# Revit family: BIM Motala Hissar
name_source: partatom
category: Generic Models
units: mm (PartAtom-declared; Revit-internal decimal feet)

## family parameters
Always vertical = Yes
Can host rebar = No
Cut with Voids When Loaded = No
Maintain Annotation Orientation = No
Part Type = Normal
Room Calculation Point = No
Round Connector Dimension = Use Diameter
Shared = No
Work Plane-Based = No

## types (1)
- MasterType
    Default Elevation = 0 mm  [stored 0 ft]
    DoorAutoTypes = 0&34603&34603&0&0&0&0&0&0&0&0&0&0&¤34603&0&0&0&0&0&0&0&0&0&0&0&0&¤0&0&0&0&0&0&0&0&0&0&0&0&0&¤0&0&0&0&0&0&0&0&0&0&0&0&0&¤
    Justerings = 0&0&0&0&0&0&0&0&0&0&0&0&0&¤34401&0&0&0&0&0&0&0&0&0&0&0&0&¤0&0&0&0&0&0&0&0&0&0&0&0&0&¤0&0&0&0&0&0&0&0&0&0&0&0&0&¤
    LeftHangTypes = 0&34101&34101&0&0&0&0&0&0&0&0&0&0&¤34101&0&0&0&0&0&0&0&0&0&0&0&0&¤0&0&0&0&0&0&0&0&0&0&0&0&0&¤0&0&0&0&0&0&0&0&0&0&0&0&0&¤
    doorHeights = 0&2260&2160&0&0&0&0&0&0&0&0&0&0&¤2260&0&2160&0&0&0&0&0&0&0&0&0&0&¤0&0&2160&0&0&0&0&0&0&0&0&0&0&¤0&0&2160&0&0&0&0&0&0&0&0&0&0&¤
    doorWidths = 900&900&900&0&0&0&0&0&0&0&0&0&0&¤1000&900&1000&0&0&0&0&0&0&0&0&0&0&¤900&900&900&0&0&0&0&0&0&0&0&0&0&¤900&900&1000&0&0&0&0&0&0&0&0&0&0&¤
    driveSide = D
    glassLists = <blob elided: 1217 chars, md5=ff18d122>
    glazingOffsets = 0&0&0&0&0&0&0&0&0&0&0&0&0&0&0&0&0&0&0&0&0&0&0&0&0&0&0&0&0&0&0&0&0&0&0&0&0&0&0&0&0&0&0&0&0&0&0&0&0&0&
    intHeights = 2000&2000&2000&0&0&0&0&0&0&0&0&0&0&¤2000&2000&2000&0&0&0&0&0&0&0&0&0&0&¤2000&2000&2000&0&0&0&0&0&0&0&0&0&0&¤2000&2000&2000&0&0&0&0&0&0&0&0&0&0&¤
    noOfStops = 3
    pitDepth = 60 mm  [stored 0.19685 ft]
    shaftDepth = 1560 mm  [stored 5.11811 ft]
    shaftHeight = 8853 mm  [stored 29.0453 ft]
    shaftWidth = 1250 mm  [stored 4.10105 ft]
    types = 0&34004&34006&0&0&0&0&0&0&0&0&0&0&¤34006&0&0&0&0&0&0&0&0&0&0&0&0&¤0&0&0&0&0&0&0&0&0&0&0&0&0&¤0&0&0&0&0&0&0&0&0&0&0&0&0&¤
    zStartPositions = 0&3268&6587&0&0&0&0&0&0&0&0&0&0&

note: [stored X ft] marks values corroborated as IEEE doubles in the binary element streams (Revit-internal decimal feet)

## geometry (parser evidence)
native form markers: Sweep x14
no freeform markers — native parametric forms only
